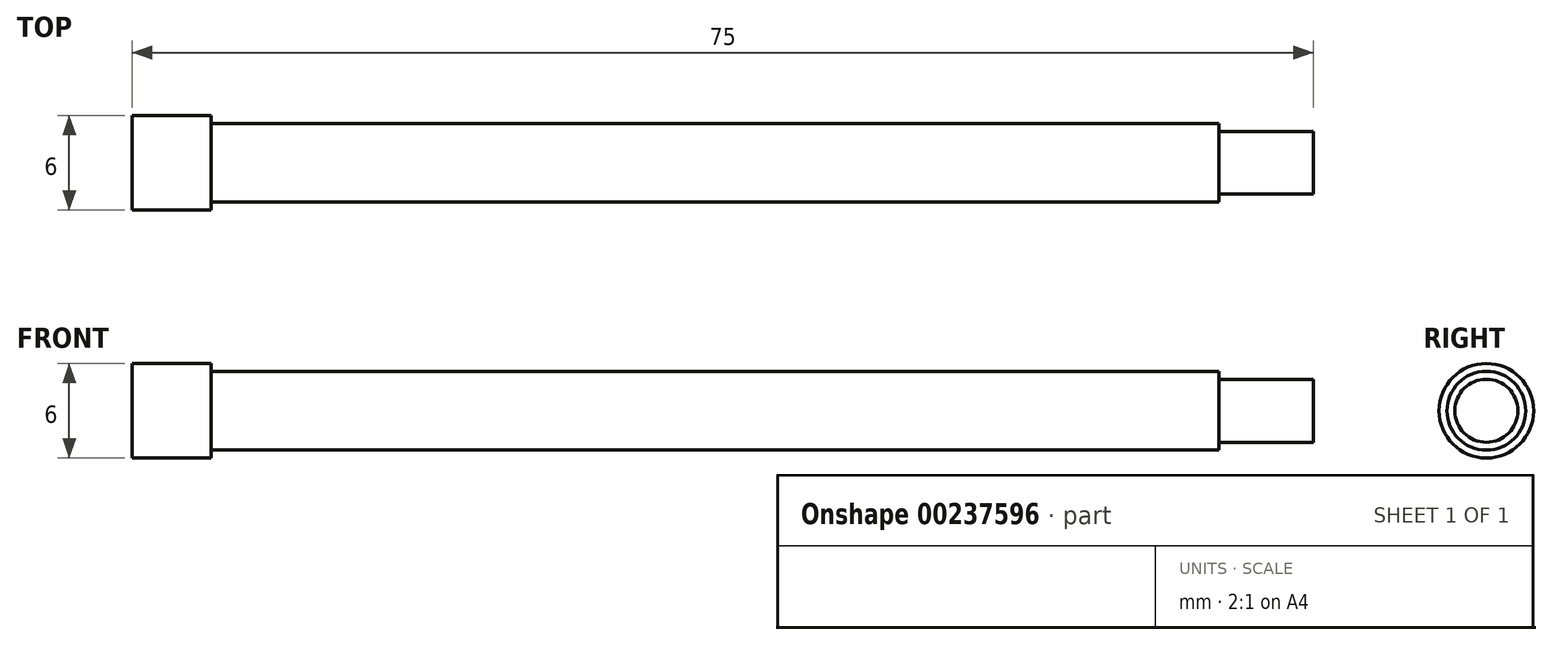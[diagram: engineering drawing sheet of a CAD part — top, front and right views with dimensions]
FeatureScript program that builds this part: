
annotation { "Feature Type Name" : "Feature", "Feature Type Description" : "" }
export const myFeature = defineFeature(function(context is Context, id is Id, definition is map)
    precondition{}
    {
        {
            var Q0;
            Q0=qCreatedBy(makeId("Front.planeOp"),FACE);
            var sketch = newSketch(context, id + "F0", { "sketchPlane" : qUnion([Q0])});
            skLineSegment(sketch, "E0", {"start": v(0, 0) * mm, "end": v(0, 3) * mm});
            skLineSegment(sketch, "E1", {"start": v(0, 3) * mm, "end": v(5, 3) * mm});
            skLineSegment(sketch, "E2", {"start": v(5, 3) * mm, "end": v(5, 2.5) * mm});
            skLineSegment(sketch, "E3", {"start": v(5, 2.5) * mm, "end": v(69, 2.5) * mm});
            skLineSegment(sketch, "E4", {"start": v(69, 2.5) * mm, "end": v(69, 2) * mm});
            skLineSegment(sketch, "E5", {"start": v(69, 2) * mm, "end": v(75, 2) * mm});
            skLineSegment(sketch, "E6", {"start": v(75, 2) * mm, "end": v(75, 0) * mm});
            skLineSegment(sketch, "E7", {"start": v(75, 0) * mm, "end": v(0, 0) * mm});
            skLineSegment(sketch, "E8", {"start": v(-9.34, 0) * mm, "end": v(84.41, 0) * mm, "construction": true});
            skSolve(sketch);
        }
        {
            var Q0;
            Q0=makeQuery(id+"F0.imprint","IMPRINT",FACE,{"disambiguationData":[TD([[makeQuery(id+"F0.imprint","IMPRINT",EDGE,{"derivedFrom":sQuery(id+"F0.wireOp",EDGE,"E0")}),-1.0]])]});
            var Q1;
            Q1=sQuery(id+"F0.wireOp",EDGE,"E8");
            revolve(context, id + "F1", {"entities" : qUnion([Q0]), "axis" : qUnion([Q1]), "revolveType" : RevolveType.FULL});
        }
    });
